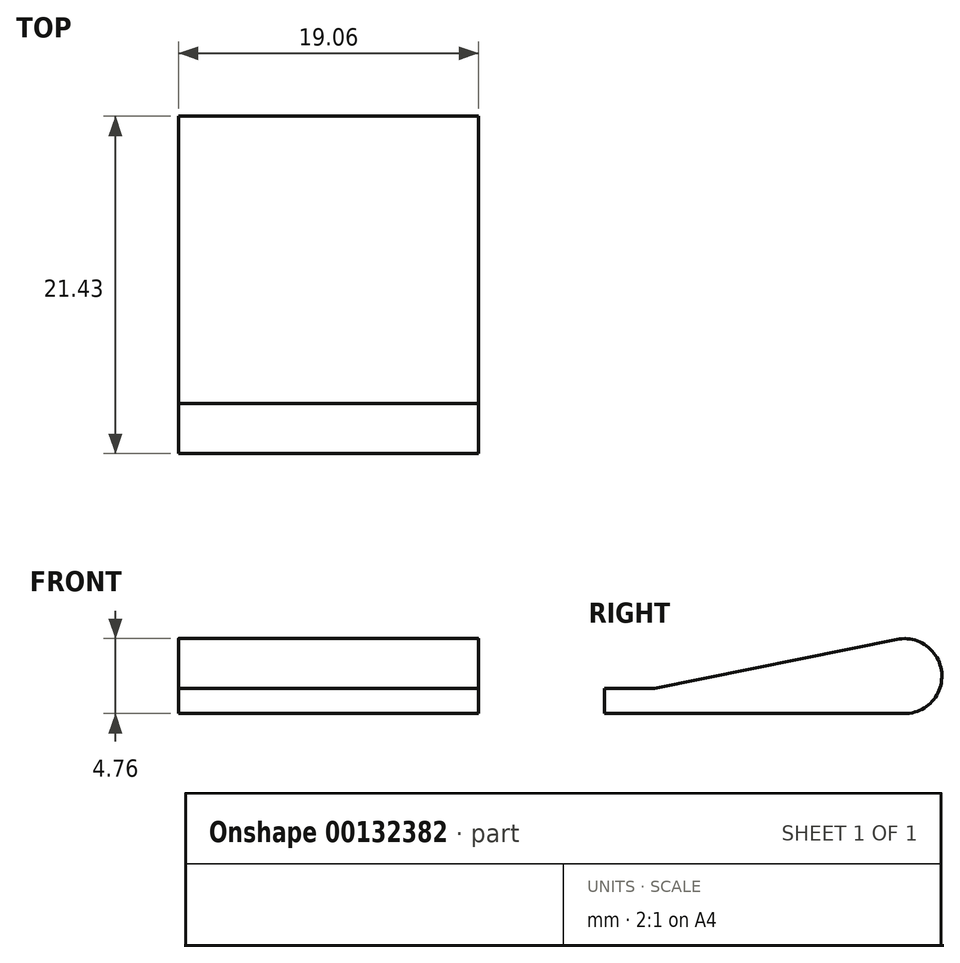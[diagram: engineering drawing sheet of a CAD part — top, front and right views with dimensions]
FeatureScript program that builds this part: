
annotation { "Feature Type Name" : "Feature", "Feature Type Description" : "" }
export const myFeature = defineFeature(function(context is Context, id is Id, definition is map)
    precondition{}
    {
        {
            var Q0;
            Q0=qCreatedBy(makeId("Right.planeOp"),FACE);
            var sketch = newSketch(context, id + "F0", { "sketchPlane" : qUnion([Q0])});
            skArc(sketch, "E0", {"start": v(0, -2.38) * mm, "mid": v(2.37, 0.24) * mm, "end": v(-0.47, 2.33) * mm});
            skLineSegment(sketch, "E1", {"start": v(0, -2.38) * mm, "end": v(-19.05, -2.38) * mm});
            skLineSegment(sketch, "E2", {"start": v(-15.88, -0.8) * mm, "end": v(-19.05, -0.8) * mm});
            skLineSegment(sketch, "E3", {"start": v(-19.05, -2.38) * mm, "end": v(-19.05, -0.8) * mm});
            skLineSegment(sketch, "E4", {"start": v(-15.88, -0.8) * mm, "end": v(-0.47, 2.33) * mm});
            skSolve(sketch);
        }
        {
            var Q0;
            Q0 = qSketchRegion(id + "F0", true);
            extrude(context, id + "F1", {"entities" : qUnion([Q0]), "endBound" : BoundingType.SYMMETRIC, "depth" : 19.05 * mm});
        }
        {
            var Q0;
            Q0=makeQuery(id+"F1.opExtrude","SWEPT_FACE",FACE,{"disambiguationData":[OSD([sQuery(id+"F0.wireOp",EDGE,"E1")])]});
            cPlane(context, id + "F2", {"entities" : qUnion([Q0]), "cplaneType" : CPlaneType.OFFSET, "offset" : 0 * mm, "width" : 152.4 * mm, "height" : 152.4 * mm});
        }
    });
